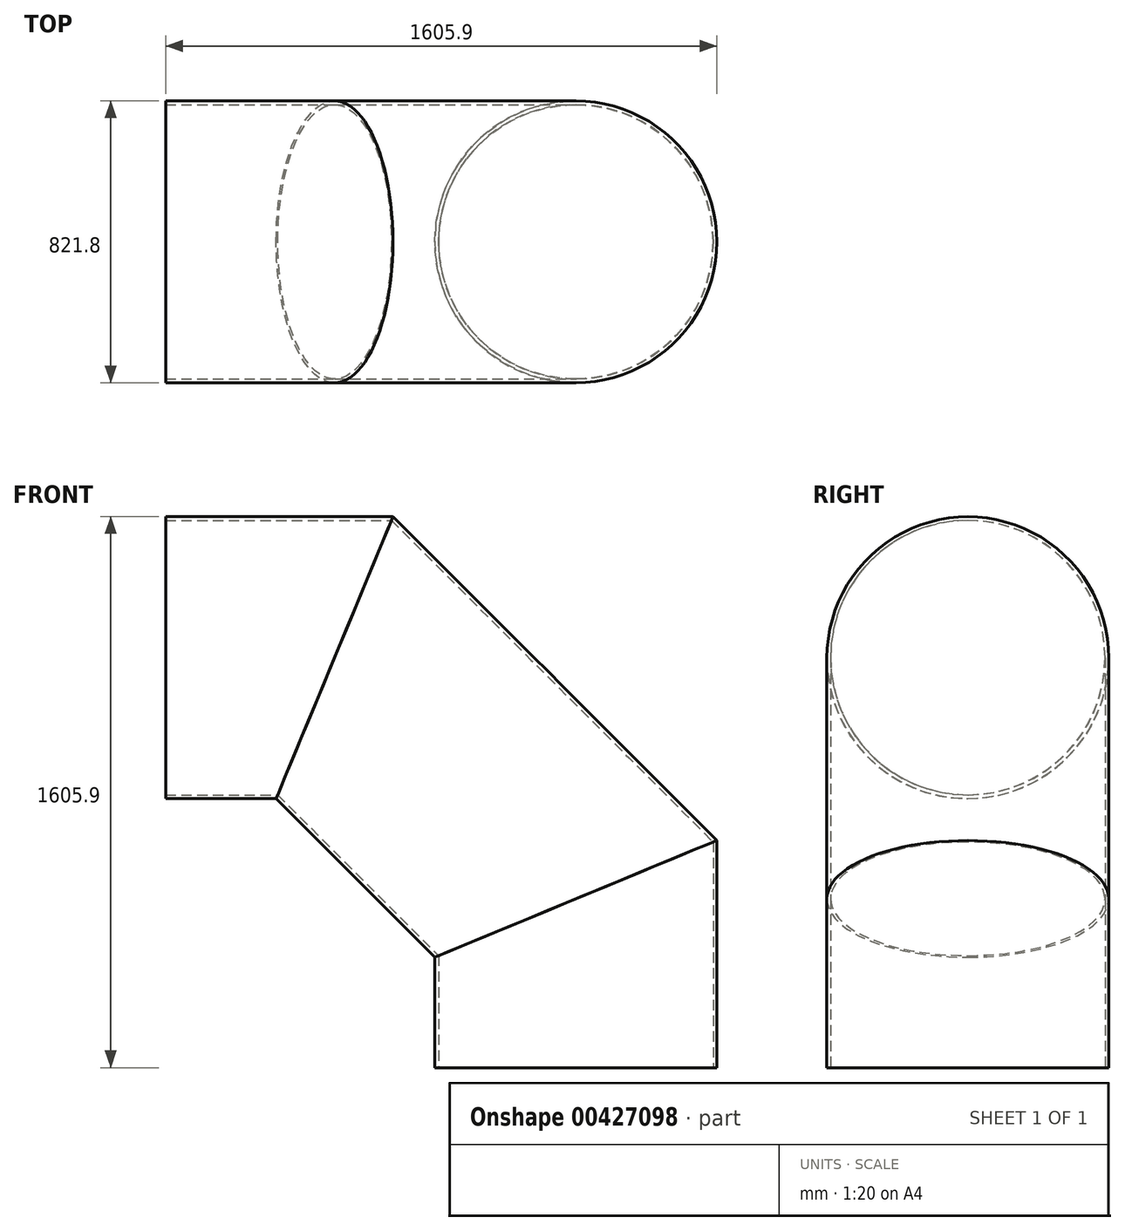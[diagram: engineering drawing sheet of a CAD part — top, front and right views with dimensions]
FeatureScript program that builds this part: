
annotation { "Feature Type Name" : "Feature", "Feature Type Description" : "" }
export const myFeature = defineFeature(function(context is Context, id is Id, definition is map)
    precondition{}
    {
        {
            var Q0;
            Q0=qCreatedBy(makeId("Front.planeOp"),FACE);
            var sketch = newSketch(context, id + "F0", { "sketchPlane" : qUnion([Q0])});
            skLineSegment(sketch, "E0", {"start": v(5, 1200) * mm, "end": v(497.06, 1200) * mm});
            skLineSegment(sketch, "E1", {"start": v(497.06, 1200) * mm, "end": v(1200, 497.06) * mm});
            skLineSegment(sketch, "E2", {"start": v(1200, 5) * mm, "end": v(1200, 497.06) * mm});
            skCircle(sketch, "E3", {"center": v(0, 0) * mm, "radius": 1200 * mm});
            skLineSegment(sketch, "E4", {"start": v(1200, -497.06) * mm, "end": v(789.1, -497.06) * mm});
            skLineSegment(sketch, "E5", {"start": v(789.1, -497.06) * mm, "end": v(789.1, 327) * mm});
            skLineSegment(sketch, "E6", {"start": v(789.1, 327) * mm, "end": v(327, 789.1) * mm});
            skLineSegment(sketch, "E7", {"start": v(327, 789.1) * mm, "end": v(-497.06, 789.1) * mm});
            skLineSegment(sketch, "E8", {"start": v(-497.06, 789.1) * mm, "end": v(-497.06, 1200) * mm});
            skLineSegment(sketch, "E9", {"start": v(-52.6, 0) * mm, "end": v(1200, 0) * mm, "construction": true});
            skLineSegment(sketch, "E10", {"start": v(0, 0) * mm, "end": v(0, 1200) * mm, "construction": true});
            skLineSegment(sketch, "E11", {"start": v(0, 0) * mm, "end": v(848.53, 848.53) * mm, "construction": true});
            skLineSegment(sketch, "E12", {"start": v(789.1, 285) * mm, "end": v(1044.04, 285) * mm, "construction": true});
            skSolve(sketch);
        }
        {
            var Q0;
            Q0=sQuery(id+"F0.wireOp",VERTEX,"E0.start");
            var Q1;
            Q1=sQuery(id+"F0.wireOp",EDGE,"E0");
            cPlane(context, id + "F1", {"entities" : qUnion([Q0, Q1]), "cplaneType" : CPlaneType.LINE_POINT, "offset" : 0 * mm, "oppositeDirection" : true, "width" : 150 * mm, "height" : 150 * mm});
        }
        {
            var Q0;
            Q0=qCreatedBy(id+"F1.planeOp",FACE);
            var sketch = newSketch(context, id + "F2", { "sketchPlane" : qUnion([Q0])});
            skCircle(sketch, "E13", {"center": v(0, 1200) * mm, "radius": 410.9 * mm});
            skCircle(sketch, "E14", {"center": v(0, 1200) * mm, "radius": 400 * mm});
            skSolve(sketch);
        }
        {
            var Q0;
            Q0=makeQuery(id+"F2.imprint","IMPRINT",FACE,{"disambiguationData":[TD([[makeQuery(id+"F2.imprint","IMPRINT",EDGE,{"derivedFrom":sQuery(id+"F2.wireOp",EDGE,"E13")}),1.0]])]});
            var Q1;
            Q1=sQuery(id+"F2.wireOp",EDGE,"E13");
            var Q2;
            Q2=sQuery(id+"F0.wireOp",EDGE,"E0");
            var Q3;
            Q3=sQuery(id+"F0.wireOp",EDGE,"E1");
            var Q4;
            Q4=sQuery(id+"F0.wireOp",EDGE,"E2");
            sweep(context, id + "F3", {"profiles" : qUnion([Q0]), "surfaceProfiles" : qUnion([Q1]), "path" : qUnion([Q2, Q3, Q4])});
        }
    });
